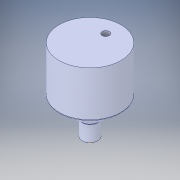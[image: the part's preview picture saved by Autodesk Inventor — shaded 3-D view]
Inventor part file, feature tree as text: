
AUTODESK INVENTOR PART (.ipt)
format: ipt  version: 2018 (Build 220112000, 112)  size: 275,456 bytes
history: native  units: in
note: dims shown in document units (in); Inventor stores cm internally (conversion verified against a paired STEP export)
features: sketch x12, extrude x12, fillet x4, projected_geometry x4, other x4, plane x2, loft x2, pattern_circular x1, chamfer x1
ambient origin geometry x8: Origin, YZ Plane, XZ Plane, XY Plane, X Axis, Y Axis, Z Axis, Center Point
bodies: Solid1 (feature_tree)
feature tree (42):
  plane  "Work Plane1"
  sketch  "Sketch1"  dims[d0=0.3937in d1=0.0in d2=1.75in d3=0.0in]
  extrude  "Extrusion1"  Depth=1.75in TaperAngle=0.0deg
  extrude  "Extrusion2"  Depth=1.0in
  sketch  "Sketch2"  dims[d25=0.45in d26=1.0in]
  extrude  "Extrusion3"  Depth=0.25in
  sketch  "Sketch10"  dims[d35=0.5in d36=0.0in d37=0.0in d38=90.0deg]
  extrude  "Extrusion4"  TaperAngle=0.0deg  [1 undecoded]
  loft  "Loft2"
  loft  "Loft3"
  extrude  "Extrusion5"  Depth=0.481in
  fillet  "Fillet1"  Radius=0.0787in
  extrude  "Extrusion6"  Depth=0.25in TaperAngle=0.0deg
  pattern_circular  "Circular Pattern1"  Count=6  [1 undecoded]
  extrude  "Extrusion7"  Depth=0.25in TaperAngle=0.0deg
  extrude  "Extrusion8"  Depth=1.0in
  fillet  "Fillet2"  Radius=0.25in
  plane  "Work Plane3"
  sketch  "Sketch18"  dims[d61=0.45in d62=1.0in d63=0.25in d64=0.0in]
  extrude  "Extrusion9"  Depth=0.45in
  extrude  "Extrusion10"  Depth=0.25in TaperAngle=0.0deg
  extrude  "Extrusion11"  Depth=0.25in TaperAngle=0.0deg
  chamfer  "Chamfer1"  Distance=0.25in
  fillet  "Fillet3"  Radius=0.0625in
  extrude  "Extrusion12"  Depth=0.0625in
  sketch  "Sketch9"  dims[d27=0.625in d28=0.0in d34=0.25in]
  projected_geometry  "Projected Loop7"
  projected_geometry  "Projected Loop8"
  sketch  "Sketch12"  dims[d39=0.0in d40=90.0deg d41=0.0in d42=90.0deg]
  other  "Edges2"
  other  "Edges3"
  other  "Edges4"
  other  "Edges5"
  sketch  "Sketch13"  dims[d43=0.0in d44=90.0deg d45=0.25in d46=0.0in]
  sketch  "Sketch14"  dims[d47=0.125in d49=0.481in d50=0.0787in]
  sketch  "Sketch16"  dims[d51=0.0394in d52=0.25in d53=0.0in d54=2.3622in d55=2.4737in]
  sketch  "Sketch17"  dims[d58=0.0591in d59=0.25in d60=0.0in]
  projected_geometry  "Projected Loop10"
  sketch  "Sketch19"  dims[d65=0.25in d66=0.45in]
  sketch  "Sketch20"  dims[d67=1.0in d68=0.25in d69=0.0in d70=0.25in d71=0.0in d72=0.25in d73=0.0in d74=0.0625in d75=0.0787in d76=45.0deg d77=0.0625in d78=0.5in d79=0.3937in d80=0.0in]
  projected_geometry  "Projected Loop11"
  fillet  "Fillet10"  Radius=0.5in
note: 2 required parameter values undecoded (feature->parameter linkage not recoverable at this tier; creation-order binding heuristic only, values carry confidence <= 0.55)
